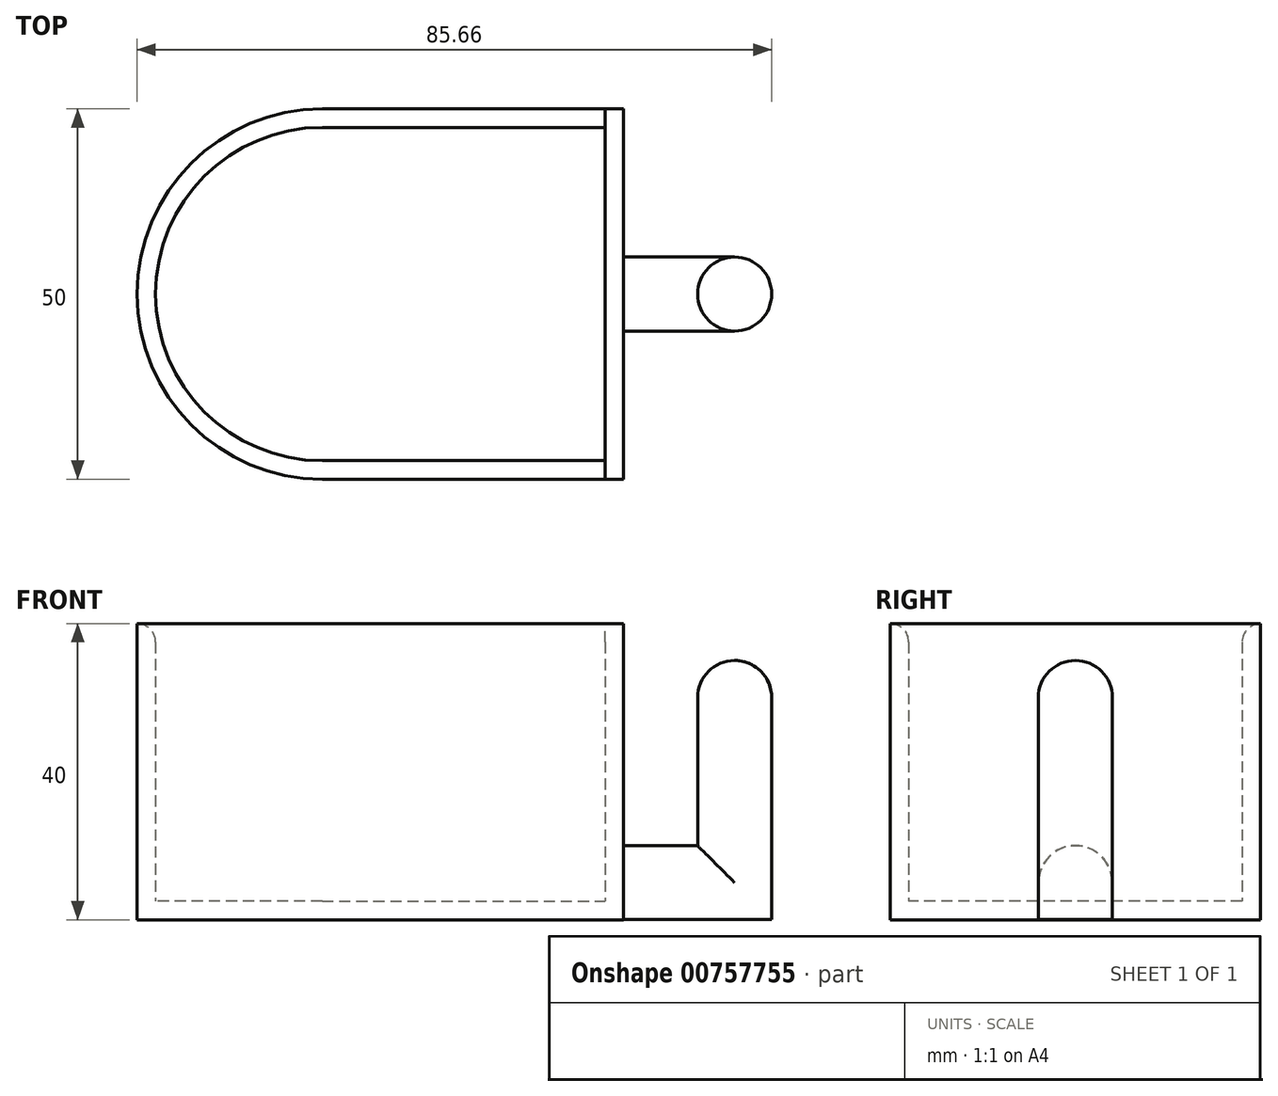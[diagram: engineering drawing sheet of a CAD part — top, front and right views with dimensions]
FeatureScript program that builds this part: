
annotation { "Feature Type Name" : "Feature", "Feature Type Description" : "" }
export const myFeature = defineFeature(function(context is Context, id is Id, definition is map)
    precondition{}
    {
        {
            var Q0;
            Q0=qCreatedBy(makeId("Top.planeOp"),FACE);
            var sketch = newSketch(context, id + "F0", { "sketchPlane" : qUnion([Q0])});
            skLineSegment(sketch, "E0", {"start": v(0, 25) * mm, "end": v(40.66, 25) * mm});
            skLineSegment(sketch, "E1", {"start": v(40.66, 25) * mm, "end": v(40.66, -25) * mm});
            skLineSegment(sketch, "E2", {"start": v(40.66, -25) * mm, "end": v(0, -25) * mm});
            skArc(sketch, "E3", {"start": v(0, 25) * mm, "mid": v(-25, 0) * mm, "end": v(0, -25) * mm});
            skSolve(sketch);
        }
        {
            var Q0;
            Q0=makeQuery(id+"F0.imprint","IMPRINT",FACE,{"disambiguationData":[TD([[makeQuery(id+"F0.imprint","IMPRINT",EDGE,{"derivedFrom":sQuery(id+"F0.wireOp",EDGE,"E0")}),-1.0]])]});
            extrude(context, id + "F1", {"entities" : qUnion([Q0]), "depth" : 40 * mm, "offsetDistance" : 25 * mm});
        }
        {
            var Q0;
            Q0=makeQuery(id+"F1.opExtrude","CAP_FACE",FACE,{"disambiguationData":[OSD([sQuery(id+"F0.wireOp",EDGE,"E0"),sQuery(id+"F0.wireOp",EDGE,"E1"),sQuery(id+"F0.wireOp",EDGE,"E2"),sQuery(id+"F0.wireOp",EDGE,"E3")])],"isStart":false});
            shell(context, id + "F2", {"entities" : qUnion([Q0]), "thickness" : 2.5 * mm});
        }
        {
            var Q0;
            Q0=makeQuery(id+"F1.opExtrude","SWEPT_FACE",FACE,{"disambiguationData":[OSD([sQuery(id+"F0.wireOp",EDGE,"E1")])]});
            var sketch = newSketch(context, id + "F3", { "sketchPlane" : qUnion([Q0])});
            skLineSegment(sketch, "E4.bottom", {"start": v(-5, 10.02) * mm, "end": v(5, 10.02) * mm});
            skLineSegment(sketch, "E4.top", {"start": v(-5, 0.02) * mm, "end": v(5, 0.02) * mm});
            skLineSegment(sketch, "E4.left", {"start": v(-5, 10.02) * mm, "end": v(-5, 0.02) * mm});
            skLineSegment(sketch, "E4.right", {"start": v(5, 10.02) * mm, "end": v(5, 0.02) * mm});
            skPoint(sketch, "E4.middle", {"position": v(0, 5.02) * mm});
            skSolve(sketch);
        }
        {
            var Q0;
            Q0=makeQuery(id+"F3.imprint","IMPRINT",FACE,{"disambiguationData":[TD([[makeQuery(id+"F3.imprint","IMPRINT",EDGE,{"derivedFrom":sQuery(id+"F3.wireOp",EDGE,"E4.bottom")}),-1.0]])]});
            extrude(context, id + "F4", {"entities" : qUnion([Q0]), "operationType" : NewBodyOperationType.ADD, "depth" : 20 * mm, "offsetDistance" : 25 * mm});
        }
        {
            var Q0;
            Q0=makeQuery(id+"F4.opExtrude","SWEPT_FACE",FACE,{"disambiguationData":[OSD([sQuery(id+"F3.wireOp",EDGE,"E4.bottom")])]});
            var sketch = newSketch(context, id + "F5", { "sketchPlane" : qUnion([Q0])});
            skLineSegment(sketch, "E5.bottom", {"start": v(60.66, -5) * mm, "end": v(50.66, -5) * mm});
            skLineSegment(sketch, "E5.top", {"start": v(60.66, 5) * mm, "end": v(50.66, 5) * mm});
            skLineSegment(sketch, "E5.left", {"start": v(60.66, -5) * mm, "end": v(60.66, 5) * mm});
            skLineSegment(sketch, "E5.right", {"start": v(50.66, -5) * mm, "end": v(50.66, 5) * mm});
            skSolve(sketch);
        }
        {
            var Q0;
            Q0=makeQuery(id+"F5.imprint","IMPRINT",FACE,{"disambiguationData":[TD([[makeQuery(id+"F5.imprint","IMPRINT",EDGE,{"derivedFrom":sQuery(id+"F5.wireOp",EDGE,"E5.bottom")}),-1.0]])]});
            extrude(context, id + "F6", {"entities" : qUnion([Q0]), "operationType" : NewBodyOperationType.ADD, "depth" : 25 * mm, "offsetDistance" : 25 * mm});
        }
        {
            var Q0;
            Q0=makeQuery(id+"F4.opExtrude","SWEPT_EDGE",EDGE,{"disambiguationData":[OSD([sQuery(id+"F3.wireOp",EDGE,"E4.bottom"),sQuery(id+"F3.wireOp",EDGE,"E4.left")])]});
            var Q1;
            Q1=makeQuery(id+"F4.opExtrude","SWEPT_EDGE",EDGE,{"disambiguationData":[OSD([sQuery(id+"F3.wireOp",EDGE,"E4.bottom"),sQuery(id+"F3.wireOp",EDGE,"E4.right")])]});
            var Q2;
            Q2=makeQuery(id+"F6.opExtrude","SWEPT_EDGE",EDGE,{"disambiguationData":[OSD([sQuery(id+"F3.wireOp",EDGE,"E4.bottom"),sQuery(id+"F3.wireOp",EDGE,"E4.left"),sQuery(id+"F5.wireOp",EDGE,"E5.bottom"),sQuery(id+"F5.wireOp",EDGE,"E5.right")])]});
            var Q3;
            Q3=makeQuery(id+"F6.opExtrude","SWEPT_EDGE",EDGE,{"disambiguationData":[OSD([sQuery(id+"F3.wireOp",EDGE,"E4.bottom"),sQuery(id+"F3.wireOp",EDGE,"E4.right"),sQuery(id+"F5.wireOp",EDGE,"E5.top"),sQuery(id+"F5.wireOp",EDGE,"E5.right")])]});
            var Q4;
            Q4=makeQuery(id+"F6.opExtrude","CAP_FACE",FACE,{"disambiguationData":[OSD([sQuery(id+"F5.wireOp",EDGE,"E5.bottom"),sQuery(id+"F5.wireOp",EDGE,"E5.top"),sQuery(id+"F5.wireOp",EDGE,"E5.left"),sQuery(id+"F5.wireOp",EDGE,"E5.right")])],"isStart":false});
            var Q5;
            Q5=makeQuery(id+"F6.boolean.opBoolean","MERGE",EDGE,{"derivedFrom":[makeQuery(id+"F4.opExtrude","CAP_EDGE",EDGE,{"disambiguationData":[OSD([sQuery(id+"F3.wireOp",EDGE,"E4.left")])],"isStart":false}),makeQuery(id+"F6.opExtrude","SWEPT_EDGE",EDGE,{"disambiguationData":[OSD([sQuery(id+"F5.wireOp",EDGE,"E5.bottom"),sQuery(id+"F5.wireOp",EDGE,"E5.left")])]})]});
            var Q6;
            Q6=makeQuery(id+"F6.boolean.opBoolean","MERGE",EDGE,{"derivedFrom":[makeQuery(id+"F4.opExtrude","CAP_EDGE",EDGE,{"disambiguationData":[OSD([sQuery(id+"F3.wireOp",EDGE,"E4.right")])],"isStart":false}),makeQuery(id+"F6.opExtrude","SWEPT_EDGE",EDGE,{"disambiguationData":[OSD([sQuery(id+"F5.wireOp",EDGE,"E5.top"),sQuery(id+"F5.wireOp",EDGE,"E5.left")])]})]});
            fillet(context, id + "F7", {"entities" : qUnion([Q0, Q1, Q2, Q3, Q4, Q5, Q6]), "radius" : 5 * mm, "tangentPropagation" : true, "allowEdgeOverflow" : false});
        }
        {
            var Q0;
            {var subQ0=sQuery(id+"F0.wireOp",EDGE,"E3");Q0=makeQuery(id+"F2.opShell","OFFSET_EDGE",EDGE,{"disambiguationData":[OSD([subQ0]),TDD([makeQuery(id+"F1.opExtrude","CAP_EDGE",EDGE,{"disambiguationData":[OSD([subQ0])],"isStart":false})])]});}
            fillet(context, id + "F8", {"entities" : qUnion([Q0]), "radius" : 2.5 * mm, "tangentPropagation" : true, "allowEdgeOverflow" : false});
        }
    });
